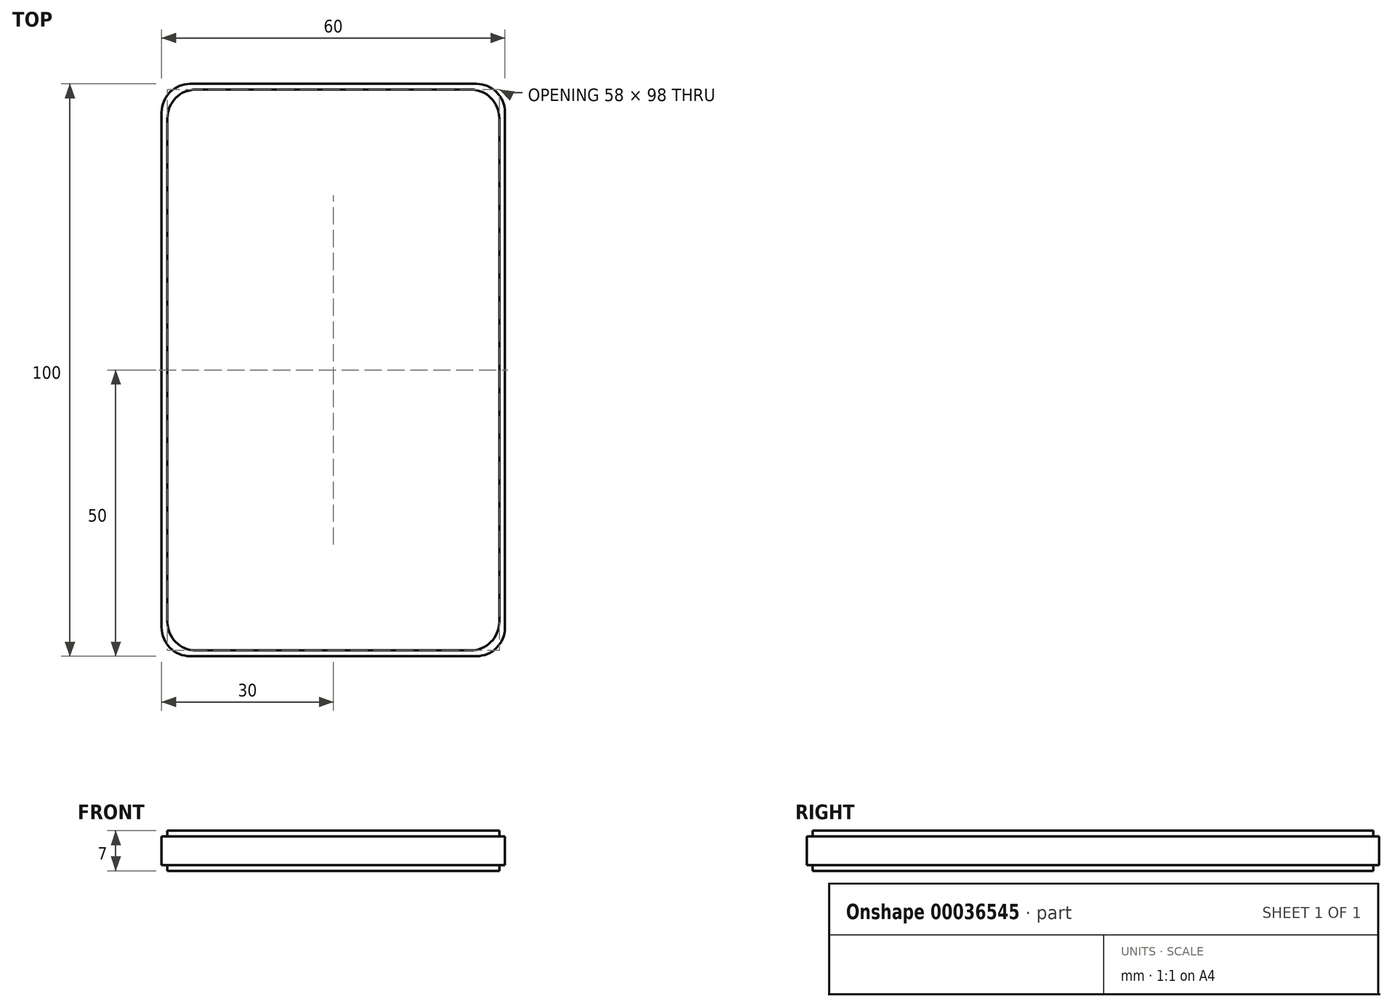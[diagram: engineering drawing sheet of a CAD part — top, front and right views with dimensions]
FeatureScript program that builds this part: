
annotation { "Feature Type Name" : "Feature", "Feature Type Description" : "" }
export const myFeature = defineFeature(function(context is Context, id is Id, definition is map)
    precondition{}
    {
        {
            var Q0;
            Q0=qCreatedBy(makeId("Top.planeOp"),FACE);
            var sketch = newSketch(context, id + "F0", { "sketchPlane" : qUnion([Q0])});
            skLineSegment(sketch, "E0", {"start": v(-30, 0) * mm, "end": v(-30, 45) * mm});
            skLineSegment(sketch, "E1", {"start": v(-25, 50) * mm, "end": v(25, 50) * mm});
            skLineSegment(sketch, "E2", {"start": v(30, 45) * mm, "end": v(30, 0) * mm});
            skLineSegment(sketch, "E3", {"start": v(-30, 0) * mm, "end": v(-30, -45) * mm});
            skLineSegment(sketch, "E4", {"start": v(-25, -50) * mm, "end": v(25, -50) * mm});
            skLineSegment(sketch, "E5", {"start": v(30, -45) * mm, "end": v(30, 0) * mm});
            skPoint(sketch, "E6.visualSharp", {"position": v(-30, 50) * mm});
            skArc(sketch, "E6.filletArc", {"start": v(-25, 50) * mm, "mid": v(-28.54, 48.54) * mm, "end": v(-30, 45) * mm});
            skPoint(sketch, "E7.visualSharp", {"position": v(30, 50) * mm});
            skArc(sketch, "E7.filletArc", {"start": v(30, 45) * mm, "mid": v(28.54, 48.54) * mm, "end": v(25, 50) * mm});
            skPoint(sketch, "E8.visualSharp", {"position": v(-30, -50) * mm});
            skArc(sketch, "E8.filletArc", {"start": v(-30, -45) * mm, "mid": v(-28.54, -48.54) * mm, "end": v(-25, -50) * mm});
            skPoint(sketch, "E9.visualSharp", {"position": v(30, -50) * mm});
            skArc(sketch, "E9.filletArc", {"start": v(25, -50) * mm, "mid": v(28.54, -48.54) * mm, "end": v(30, -45) * mm});
            skPoint(sketch, "E10.endSnap0", {"position": v(0, 50) * mm});
            skLineSegment(sketch, "E11", {"start": v(-29, 0) * mm, "end": v(-29, -44) * mm});
            skLineSegment(sketch, "E12", {"start": v(-24, -49) * mm, "end": v(0, -49) * mm});
            skLineSegment(sketch, "E13.MirrorCS", {"start": v(-29, 0) * mm, "end": v(-29, 44) * mm});
            skLineSegment(sketch, "E14.MirrorCS", {"start": v(-24, 49) * mm, "end": v(0, 49) * mm});
            skLineSegment(sketch, "E15.MirrorCS", {"start": v(29, 0) * mm, "end": v(29, 44) * mm});
            skLineSegment(sketch, "E16.MirrorCS", {"start": v(24, 49) * mm, "end": v(0, 49) * mm});
            skLineSegment(sketch, "E17.MirrorCS", {"start": v(29, 0) * mm, "end": v(29, -44) * mm});
            skLineSegment(sketch, "E18.MirrorCS", {"start": v(24, -49) * mm, "end": v(0, -49) * mm});
            skPoint(sketch, "E19.visualSharp", {"position": v(-29, -49) * mm});
            skArc(sketch, "E19.filletArc", {"start": v(-29, -44) * mm, "mid": v(-27.54, -47.54) * mm, "end": v(-24, -49) * mm});
            skPoint(sketch, "E20.visualSharp", {"position": v(29, -49) * mm});
            skArc(sketch, "E20.filletArc", {"start": v(24, -49) * mm, "mid": v(27.54, -47.54) * mm, "end": v(29, -44) * mm});
            skPoint(sketch, "E21.visualSharp", {"position": v(29, 49) * mm});
            skArc(sketch, "E21.filletArc", {"start": v(29, 44) * mm, "mid": v(27.54, 47.54) * mm, "end": v(24, 49) * mm});
            skPoint(sketch, "E22.visualSharp", {"position": v(-29, 49) * mm});
            skArc(sketch, "E22.filletArc", {"start": v(-24, 49) * mm, "mid": v(-27.54, 47.54) * mm, "end": v(-29, 44) * mm});
            skSolve(sketch);
        }
        {
            var Q0;
            Q0=makeQuery(id+"F0.imprint","IMPRINT",FACE,{"disambiguationData":[TD([[makeQuery(id+"F0.imprint","IMPRINT",EDGE,{"derivedFrom":sQuery(id+"F0.wireOp",EDGE,"E11")}),1.0]])]});
            extrude(context, id + "F1", {"entities" : qUnion([Q0]), "depth" : 1 * mm});
        }
        {
            var Q0;
            Q0=makeQuery(id+"F0.imprint","IMPRINT",FACE,{"disambiguationData":[TD([[makeQuery(id+"F0.imprint","IMPRINT",EDGE,{"derivedFrom":sQuery(id+"F0.wireOp",EDGE,"E0")}),-1.0]])]});
            var Q1;
            Q1=makeQuery(id+"F0.imprint","IMPRINT",FACE,{"disambiguationData":[TD([[makeQuery(id+"F0.imprint","IMPRINT",EDGE,{"derivedFrom":sQuery(id+"F0.wireOp",EDGE,"E11")}),1.0]])]});
            extrude(context, id + "F2", {"entities" : qUnion([Q0, Q1]), "operationType" : NewBodyOperationType.ADD, "oppositeDirection" : true, "depth" : 5 * mm});
        }
        {
            var Q0;
            Q0=makeQuery(id+"F1.opExtrude","CAP_FACE",FACE,{"disambiguationData":[OSD([sQuery(id+"F0.wireOp",EDGE,"E11"),sQuery(id+"F0.wireOp",EDGE,"E12"),sQuery(id+"F0.wireOp",EDGE,"E13.MirrorCS"),sQuery(id+"F0.wireOp",EDGE,"E14.MirrorCS"),sQuery(id+"F0.wireOp",EDGE,"E15.MirrorCS"),sQuery(id+"F0.wireOp",EDGE,"E16.MirrorCS"),sQuery(id+"F0.wireOp",EDGE,"E17.MirrorCS"),sQuery(id+"F0.wireOp",EDGE,"E18.MirrorCS"),sQuery(id+"F0.wireOp",EDGE,"E19.filletArc"),sQuery(id+"F0.wireOp",EDGE,"E20.filletArc"),sQuery(id+"F0.wireOp",EDGE,"E21.filletArc"),sQuery(id+"F0.wireOp",EDGE,"E22.filletArc")])],"isStart":false});
            extrude(context, id + "F3", {"entities" : qUnion([Q0]), "operationType" : NewBodyOperationType.ADD, "oppositeDirection" : true, "depth" : 7 * mm});
        }
    });
